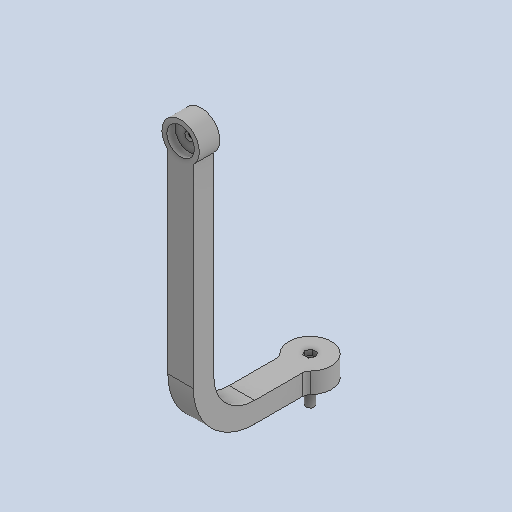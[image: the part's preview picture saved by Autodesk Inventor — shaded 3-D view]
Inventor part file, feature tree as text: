
AUTODESK INVENTOR PART (.ipt)
format: ipt  version: 2024 (Build 280153000, 153)  size: 331,776 bytes
history: native  units: mm
features: sketch x9, extrude x7, other x3, sweep x1, plane x1, mirror x1
ambient origin geometry x8: Origin, YZ Plane, XZ Plane, XY Plane, X Axis, Y Axis, Z Axis, Center Point
bodies: Solid1 (feature_tree)
feature tree (22):
  extrude  "Extrusion1"  Depth=12.0mm TaperAngle=0.0deg
  sweep  "Sweep2"
  plane  "Work Plane11"
  extrude  "Extrusion17"  TaperAngle=90.0deg  [1 undecoded]
  extrude  "Extrusion18"  TaperAngle=0.0deg  [1 undecoded]
  other  "Work Point1"
  extrude  "Extrusion20"  Depth=12.0mm TaperAngle=0.0deg
  extrude  "Extrusion21"  TaperAngle=0.0deg  [1 undecoded]
  mirror  "Mirror2"
  extrude  "Extrusion22"  Depth=10.0mm
  extrude  "Extrusion23"  Depth=26.0mm TaperAngle=0.0deg
  sketch  "Sketch1"  dims[d0=25.0mm d1=12.0mm d2=0.0mm]
  sketch  "Sketch22"  dims[d109=5.0mm d110=50.0mm]
  sketch  "Sketch23"  dims[d111=140.010783mm d112=90.0deg]
  sketch  "Sketch24"  dims[d113=30.0mm d114=0.0mm d115=0.0mm]
  sketch  "Sketch25"  dims[d116=-6.0mm d121=12.0mm d122=0.0mm]
  other  "Work Axis1"
  other  "Work Axis2"
  sketch  "Sketch27"  dims[d123=5.0mm d124=0.0mm d125=0.0mm]
  sketch  "Sketch28"  dims[d129=15.0mm d131=10.0mm]
  sketch  "Sketch29"  dims[d136=4.8mm d137=26.0mm d138=0.0mm]
  sketch  "Sketch30"  dims[d139=22.0mm d140=12.0mm d141=15.0mm d142=16.2mm d143=5.0mm d144=0.0mm d145=5.5mm d146=3.0mm d147=0.0mm d148=3.2mm d149=0.0mm d150=0.0mm d74=0.5mm d75=0.872665mm d76=0.5mm d77=0.872665mm d98=0.0mm d99=0.0mm d100=0.0mm d101=0.0mm d102=0.872665mm d103=0.5mm d104=0.872665mm]
note: 3 required parameter values undecoded (feature->parameter linkage not recoverable at this tier; creation-order binding heuristic only, values carry confidence <= 0.55)
